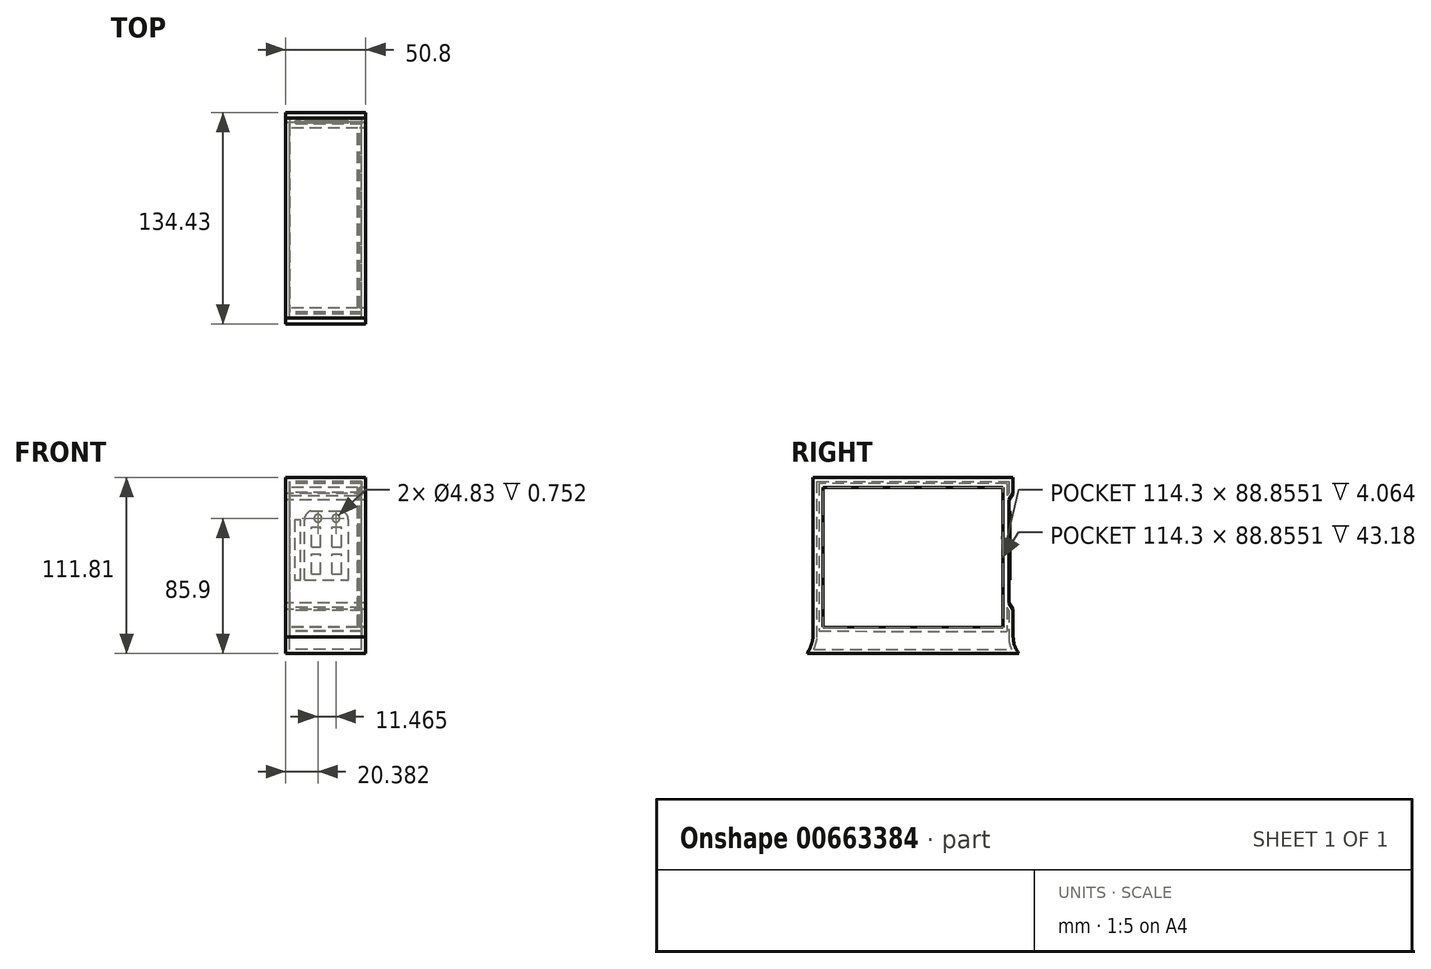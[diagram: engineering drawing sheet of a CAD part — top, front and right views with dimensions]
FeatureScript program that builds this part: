
annotation { "Feature Type Name" : "Feature", "Feature Type Description" : "" }
export const myFeature = defineFeature(function(context is Context, id is Id, definition is map)
    precondition{}
    {
        {
            var Q0;
            Q0=qCreatedBy(makeId("Right.planeOp"),FACE);
            var sketch = newSketch(context, id + "F0", { "sketchPlane" : qUnion([Q0])});
            skLineSegment(sketch, "E0", {"start": v(-61.7, -45.44) * mm, "end": v(-61.7, 55.97) * mm});
            skLineSegment(sketch, "E1", {"start": v(-61.7, 55.97) * mm, "end": v(65.3, 55.97) * mm});
            skLineSegment(sketch, "E2", {"start": v(65.3, 55.97) * mm, "end": v(65.3, 45.81) * mm});
            skLineSegment(sketch, "E3", {"start": v(65.3, -45.59) * mm, "end": v(-61.7, -45.44) * mm});
            skLineSegment(sketch, "E4", {"start": v(-65.5, -55.84) * mm, "end": v(68.92, -55.84) * mm});
            skFitSpline(sketch, "E5", {"points": [v(-65.5, -55.84) * mm, v(-63.42, -51.67) * mm, v(-61.7, -45.44) * mm], "startDerivative": vector(4.85, 8.52) * mm, "endDerivative": vector(2.82, 12.18) * mm});
            skLineSegment(sketch, "E6.0", {"start": v(-55.35, 49.62) * mm, "end": v(58.95, 49.62) * mm});
            skLineSegment(sketch, "E6.1", {"start": v(-55.35, -39.1) * mm, "end": v(-55.35, 49.62) * mm});
            skLineSegment(sketch, "E6.2", {"start": v(58.95, -39.23) * mm, "end": v(-55.35, -39.1) * mm});
            skLineSegment(sketch, "E6.3", {"start": v(58.95, 49.62) * mm, "end": v(58.95, -39.23) * mm});
            skFitSpline(sketch, "E7", {"points": [v(68.92, -55.84) * mm, v(66.08, -50.54) * mm, v(65.3, -45.59) * mm], "startDerivative": vector(-6.4, 10.07) * mm, "endDerivative": vector(-0.74, 10.36) * mm});
            skLineSegment(sketch, "E8", {"start": v(65.3, -27.8) * mm, "end": v(65.3, -45.59) * mm});
            skLineSegment(sketch, "E9", {"start": v(65.3, -27.8) * mm, "end": v(62.5, -23.57) * mm});
            skLineSegment(sketch, "E10", {"start": v(65.3, 45.81) * mm, "end": v(62.5, 41.58) * mm});
            skLineSegment(sketch, "E11", {"start": v(62.5, 41.58) * mm, "end": v(62.5, -23.57) * mm});
            skSolve(sketch);
        }
        {
            var Q0;
            Q0 = qSketchRegion(id + "F0", true);
            extrude(context, id + "F1", {"entities" : qUnion([Q0]), "depth" : 50.8 * mm, "offsetDistance" : 25.4 * mm});
        }
        {
            var Q0;
            Q0=makeQuery(id+"F0.imprint","IMPRINT",FACE,{"disambiguationData":[TD([[makeQuery(id+"F0.imprint","IMPRINT",EDGE,{"derivedFrom":sQuery(id+"F0.wireOp",EDGE,"E6.0")}),-1.0]])]});
            extrude(context, id + "F2", {"entities" : qUnion([Q0]), "operationType" : NewBodyOperationType.ADD, "depth" : 2.54 * mm, "offsetDistance" : 25.4 * mm});
        }
        {
            var Q0;
            {var subQ0=sQuery(id+"F0.wireOp",EDGE,"E6.3");var subQ1=sQuery(id+"F0.wireOp",EDGE,"E6.2");var subQ2=sQuery(id+"F0.wireOp",EDGE,"E6.1");var subQ3=sQuery(id+"F0.wireOp",EDGE,"E6.0");Q0=makeQuery(id+"F2.boolean.opBoolean","MERGE",FACE,{"derivedFrom":[makeQuery(id+"F1.opExtrude","CAP_FACE",FACE,{"disambiguationData":[OSD([sQuery(id+"F0.wireOp",EDGE,"E0"),sQuery(id+"F0.wireOp",EDGE,"E1"),sQuery(id+"F0.wireOp",EDGE,"E2"),sQuery(id+"F0.wireOp",EDGE,"E4"),sQuery(id+"F0.wireOp",EDGE,"E5"),subQ3,subQ2,subQ1,subQ0,sQuery(id+"F0.wireOp",EDGE,"E7"),sQuery(id+"F0.wireOp",EDGE,"E8"),sQuery(id+"F0.wireOp",EDGE,"E9"),sQuery(id+"F0.wireOp",EDGE,"E10"),sQuery(id+"F0.wireOp",EDGE,"E11")])],"isStart":true}),makeQuery(id+"F2.opExtrude","CAP_FACE",FACE,{"disambiguationData":[OSD([subQ3,subQ2,subQ1,subQ0])],"isStart":true})]});}
            var Q1;
            {var subQ0=sQuery(id+"F0.wireOp",EDGE,"E6.3");var subQ1=sQuery(id+"F0.wireOp",EDGE,"E6.2");var subQ2=sQuery(id+"F0.wireOp",EDGE,"E6.1");var subQ3=sQuery(id+"F0.wireOp",EDGE,"E6.0");Q1=makeQuery(id+"FS3AL2hlnSBAwNt_1.boolean.opBoolean","MERGE",FACE,{"derivedFrom":[makeQuery(id+"F1.opExtrude","CAP_FACE",FACE,{"disambiguationData":[OSD([sQuery(id+"F0.wireOp",EDGE,"E0"),sQuery(id+"F0.wireOp",EDGE,"E1"),sQuery(id+"F0.wireOp",EDGE,"E2"),sQuery(id+"F0.wireOp",EDGE,"E4"),sQuery(id+"F0.wireOp",EDGE,"E5"),subQ3,subQ2,subQ1,subQ0,sQuery(id+"F0.wireOp",EDGE,"E7"),sQuery(id+"F0.wireOp",EDGE,"E8"),sQuery(id+"F0.wireOp",EDGE,"E9"),sQuery(id+"F0.wireOp",EDGE,"E10"),sQuery(id+"F0.wireOp",EDGE,"E11")])],"isStart":false}),makeQuery(id+"FS3AL2hlnSBAwNt_1.opThicken","CAP_FACE",FACE,{"disambiguationData":[OSD([subQ3,subQ2,subQ1,subQ0])],"isStart":true})]});}
            var Q2;
            Q2=makeQuery(id+"F1.opExtrude","SWEPT_BODY",BODY,{"disambiguationData":[OSD([sQuery(id+"F0.wireOp",EDGE,"E0"),sQuery(id+"F0.wireOp",EDGE,"E1"),sQuery(id+"F0.wireOp",EDGE,"E2"),sQuery(id+"F0.wireOp",EDGE,"E4"),sQuery(id+"F0.wireOp",EDGE,"E5"),sQuery(id+"F0.wireOp",EDGE,"E6.0"),sQuery(id+"F0.wireOp",EDGE,"E6.1"),sQuery(id+"F0.wireOp",EDGE,"E6.2"),sQuery(id+"F0.wireOp",EDGE,"E6.3"),sQuery(id+"F0.wireOp",EDGE,"E7"),sQuery(id+"F0.wireOp",EDGE,"E8"),sQuery(id+"F0.wireOp",EDGE,"E9"),sQuery(id+"F0.wireOp",EDGE,"E10"),sQuery(id+"F0.wireOp",EDGE,"E11")])]});
            shell(context, id + "F3", {"isHollow" : true, "entities" : qUnion([Q0, Q1]), "parts" : qUnion([Q2]), "thickness" : 2.54 * mm});
        }
        {
            var Q0;
            Q0=qCreatedBy(makeId("Front.planeOp"),FACE);
            var sketch = newSketch(context, id + "F4", { "sketchPlane" : qUnion([Q0])});
            skLineSegment(sketch, "E12.bottom", {"start": v(39.72, 28.92) * mm, "end": v(11.78, 28.92) * mm});
            skLineSegment(sketch, "E12.top", {"start": v(39.72, -9.18) * mm, "end": v(11.78, -9.18) * mm});
            skLineSegment(sketch, "E12.left", {"start": v(39.72, 28.92) * mm, "end": v(39.72, -9.18) * mm});
            skLineSegment(sketch, "E12.right", {"start": v(11.78, 28.92) * mm, "end": v(11.78, -9.18) * mm});
            skLineSegment(sketch, "E13", {"start": v(50.88, 41.62) * mm, "end": v(0, 41.62) * mm});
            skLineSegment(sketch, "E14.bottom", {"start": v(35.28, 24.55) * mm, "end": v(29.43, 24.55) * mm});
            skLineSegment(sketch, "E14.top", {"start": v(35.28, 11.85) * mm, "end": v(29.43, 11.85) * mm});
            skLineSegment(sketch, "E14.left", {"start": v(35.28, 24.55) * mm, "end": v(35.28, 11.85) * mm});
            skLineSegment(sketch, "E14.right", {"start": v(29.43, 24.55) * mm, "end": v(29.43, 11.85) * mm});
            skLineSegment(sketch, "E15.bottom", {"start": v(22.07, 24.55) * mm, "end": v(16.23, 24.55) * mm});
            skLineSegment(sketch, "E15.top", {"start": v(22.07, 11.85) * mm, "end": v(16.23, 11.85) * mm});
            skLineSegment(sketch, "E15.left", {"start": v(22.07, 24.55) * mm, "end": v(22.07, 11.85) * mm});
            skLineSegment(sketch, "E15.right", {"start": v(16.23, 24.55) * mm, "end": v(16.23, 11.85) * mm});
            skLineSegment(sketch, "E16.bottom", {"start": v(35.28, 7.33) * mm, "end": v(29.43, 7.33) * mm});
            skLineSegment(sketch, "E16.top", {"start": v(35.28, -5.37) * mm, "end": v(29.43, -5.37) * mm});
            skLineSegment(sketch, "E16.left", {"start": v(35.28, 7.33) * mm, "end": v(35.28, -5.37) * mm});
            skLineSegment(sketch, "E16.right", {"start": v(29.43, 7.33) * mm, "end": v(29.43, -5.37) * mm});
            skLineSegment(sketch, "E17.bottom", {"start": v(22.07, 7.33) * mm, "end": v(16.23, 7.33) * mm});
            skLineSegment(sketch, "E17.top", {"start": v(22.07, -5.37) * mm, "end": v(16.23, -5.37) * mm});
            skLineSegment(sketch, "E17.left", {"start": v(22.07, 7.33) * mm, "end": v(22.07, -5.37) * mm});
            skLineSegment(sketch, "E17.right", {"start": v(16.23, 7.33) * mm, "end": v(16.23, -5.37) * mm});
            skArc(sketch, "E18", {"start": v(39.72, 28.92) * mm, "mid": v(38.63, 32.47) * mm, "end": v(35.74, 34.8) * mm});
            skArc(sketch, "E19", {"start": v(15.76, 34.8) * mm, "mid": v(12.87, 32.47) * mm, "end": v(11.78, 28.92) * mm});
            skLineSegment(sketch, "E20", {"start": v(35.74, 34.8) * mm, "end": v(15.76, 34.8) * mm});
            skCircle(sketch, "E21", {"center": v(31.85, 30.06) * mm, "radius": 2.41 * mm});
            skCircle(sketch, "E22", {"center": v(20.38, 30.06) * mm, "radius": 2.41 * mm});
            skLineSegment(sketch, "E23", {"start": v(9.24, 28.92) * mm, "end": v(9.24, -9.18) * mm});
            skLineSegment(sketch, "E24", {"start": v(9.24, -9.18) * mm, "end": v(5.43, -9.18) * mm});
            skLineSegment(sketch, "E25", {"start": v(5.43, -9.18) * mm, "end": v(5.43, 28.92) * mm});
            skLineSegment(sketch, "E26", {"start": v(5.43, 28.92) * mm, "end": v(9.24, 28.92) * mm});
            skSolve(sketch);
        }
        {
            var Q0;
            Q0=makeQuery(id+"F2.opExtrude","CAP_FACE",FACE,{"disambiguationData":[OSD([sQuery(id+"F0.wireOp",EDGE,"E6.0"),sQuery(id+"F0.wireOp",EDGE,"E6.1"),sQuery(id+"F0.wireOp",EDGE,"E6.2"),sQuery(id+"F0.wireOp",EDGE,"E6.3")])],"isStart":false});
            extrude(context, id + "F5", {"entities" : qUnion([Q0]), "operationType" : NewBodyOperationType.ADD, "depth" : 44.2 * mm, "offsetDistance" : 25.4 * mm, "hasSecondDirection" : true, "secondDirectionOppositeDirection" : false, "secondDirectionDepth" : 43.18 * mm});
        }
        {
            var Q0;
            Q0 = qSketchRegion(id + "F4", true);
            extrude(context, id + "F6", {"entities" : qUnion([Q0]), "operationType" : NewBodyOperationType.ADD, "oppositeDirection" : true, "depth" : 63.25 * mm, "offsetDistance" : 25.4 * mm, "hasSecondDirection" : true, "secondDirectionOppositeDirection" : true, "secondDirectionDepth" : 61.72 * mm});
        }
    });
